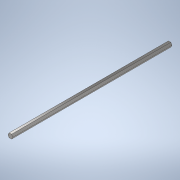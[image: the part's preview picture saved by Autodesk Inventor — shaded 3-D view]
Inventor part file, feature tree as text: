
AUTODESK INVENTOR PART (.ipt)
format: ipt  version: 2020 (Build 240168000, 168)  size: 104,448 bytes
history: native  units: in
note: dims shown in document units (in); Inventor stores cm internally (conversion verified against a paired STEP export)
features: extrude x1, sketch x1
ambient origin geometry x8: Origin, YZ Plane, XZ Plane, XY Plane, X Axis, Y Axis, Z Axis, Center Point
bodies: Solid1 (feature_tree)
feature tree (2):
  extrude  "Extrusion1"  Depth=19.0in TaperAngle=0.0deg
  sketch  "Sketch1"  dims[d0=0.5in d1=19.0in d2=0.0in]
